# Revit family: P26339A75FTB,2FTB
name_source: partatom
category: Plumbing Fixtures
revit_build: Autodesk Revit LT 2017 (Build: 20160225_1515(x64)
units: mm (PartAtom-declared; Revit-internal decimal feet)

## family parameters
Always vertical = Yes
Cut with Voids When Loaded = No
OmniClass Number = 23.45.05.14.17
OmniClass Title = Showers
Part Type = Normal
Room Calculation Point = No
Round Connector Dimension = Use Diameter
Shared = No
Work Plane-Based = No

## types (3) — shared parameters
Assembly Code = D2010710
Description = Trench Drain, Beveled Threshold
Keynote = 22 40 00.B3
Type Comments = ADA Compliant
URL = http://www.bestbath.com
Unit Width = 63"

## per-type parameters (varying)
| type | Manufacturer | Threshold Height | Unit Height |
| P26339A2FTB.V3 | best bath | 2" | 7" |
| P26339A1FTB.V3 | best bath | 1" | 6" |
| P26339A75FTB.V3 | bestbath | 3/4" | 5 3/4" |

note: column(s) folded — value = type name in every type: Model

## geometry (parser evidence)
native form markers: Blend x25, Sweep x2
no freeform markers — native parametric forms only
